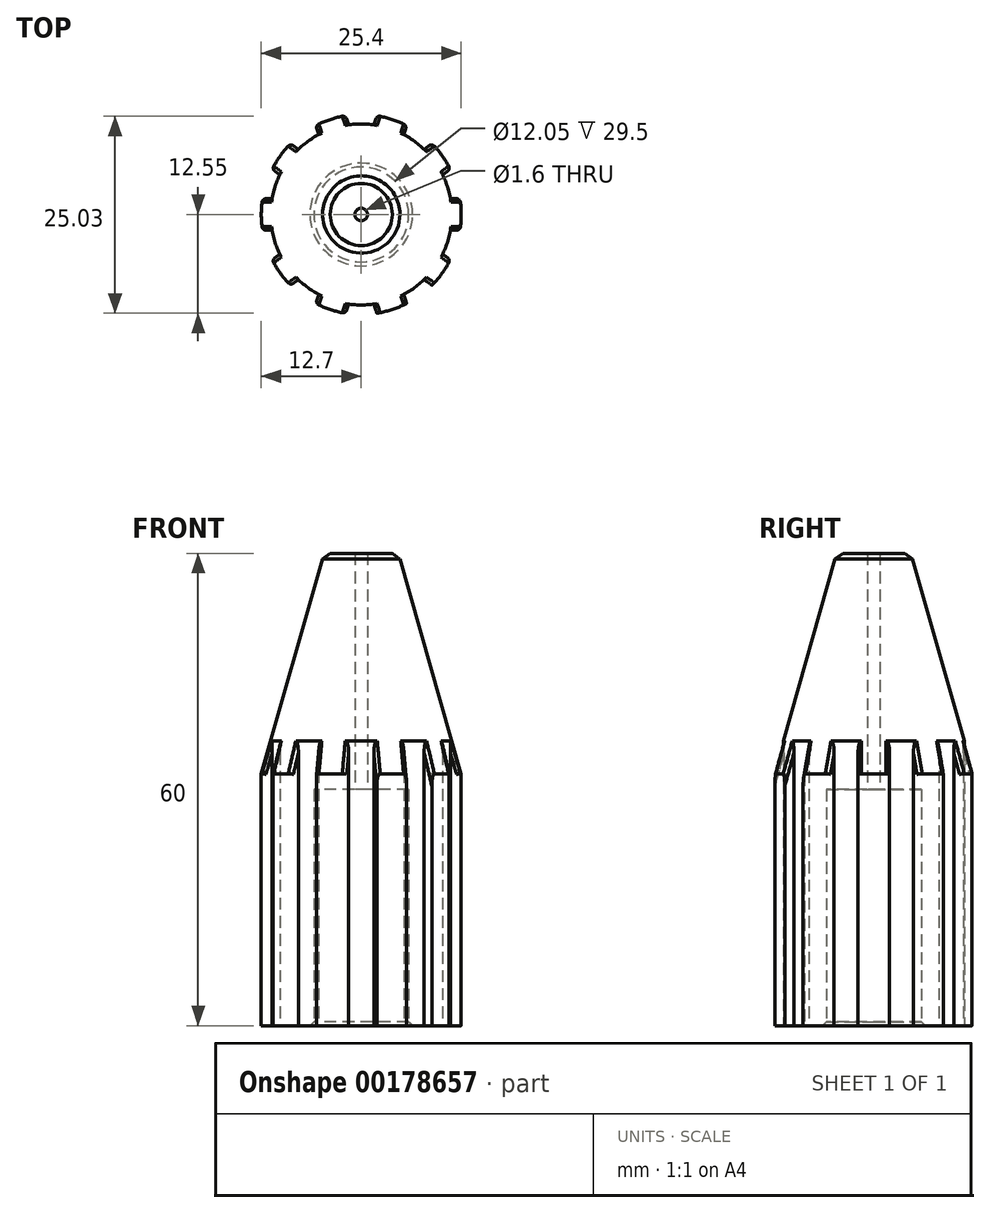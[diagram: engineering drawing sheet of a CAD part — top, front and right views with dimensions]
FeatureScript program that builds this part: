
annotation { "Feature Type Name" : "Feature", "Feature Type Description" : "" }
export const myFeature = defineFeature(function(context is Context, id is Id, definition is map)
    precondition{}
    {
        {
            var Q0;
            Q0=qCreatedBy(makeId("Top.planeOp"),FACE);
            var sketch = newSketch(context, id + "F0", { "sketchPlane" : qUnion([Q0])});
            skCircle(sketch, "E0", {"center": v(0, 0) * mm, "radius": 6.03 * mm});
            skArc(sketch, "E1", {"start": v(12.54, -2) * mm, "mid": v(12.7, 0) * mm, "end": v(12.54, 2) * mm});
            skArc(sketch, "E2", {"start": v(11.32, 2) * mm, "mid": v(10.94, 3.55) * mm, "end": v(10.34, 5.04) * mm});
            skLineSegment(sketch, "E3", {"start": v(11.32, -2) * mm, "end": v(12.54, -2) * mm});
            skLineSegment(sketch, "E4", {"start": v(11.32, 2) * mm, "end": v(12.54, 2) * mm});
            skLineSegment(sketch, "E5.1.0", {"start": v(10.34, -5.04) * mm, "end": v(11.32, -5.75) * mm});
            skArc(sketch, "E5.1.1", {"start": v(8.97, -8.99) * mm, "mid": v(10.27, -7.46) * mm, "end": v(11.32, -5.75) * mm});
            skLineSegment(sketch, "E5.1.2", {"start": v(7.99, -8.27) * mm, "end": v(8.97, -8.99) * mm});
            skLineSegment(sketch, "E5.2.0", {"start": v(5.4, -10.15) * mm, "end": v(5.78, -11.3) * mm});
            skArc(sketch, "E5.2.1", {"start": v(1.97, -12.55) * mm, "mid": v(3.92, -12.08) * mm, "end": v(5.78, -11.3) * mm});
            skLineSegment(sketch, "E5.2.2", {"start": v(1.6, -11.39) * mm, "end": v(1.97, -12.55) * mm});
            skLineSegment(sketch, "E5.3.0", {"start": v(-1.6, -11.39) * mm, "end": v(-1.97, -12.55) * mm});
            skArc(sketch, "E5.3.1", {"start": v(-5.78, -11.3) * mm, "mid": v(-3.92, -12.08) * mm, "end": v(-1.97, -12.55) * mm});
            skLineSegment(sketch, "E5.3.2", {"start": v(-5.4, -10.15) * mm, "end": v(-5.78, -11.3) * mm});
            skLineSegment(sketch, "E5.4.0", {"start": v(-7.99, -8.27) * mm, "end": v(-8.97, -8.99) * mm});
            skArc(sketch, "E5.4.1", {"start": v(-11.32, -5.75) * mm, "mid": v(-10.27, -7.46) * mm, "end": v(-8.97, -8.99) * mm});
            skLineSegment(sketch, "E5.4.2", {"start": v(-10.34, -5.04) * mm, "end": v(-11.32, -5.75) * mm});
            skLineSegment(sketch, "E5.5.0", {"start": v(-11.32, -2) * mm, "end": v(-12.54, -2) * mm});
            skArc(sketch, "E5.5.1", {"start": v(-12.54, 2) * mm, "mid": v(-12.7, 0) * mm, "end": v(-12.54, -2) * mm});
            skLineSegment(sketch, "E5.5.2", {"start": v(-11.32, 2) * mm, "end": v(-12.54, 2) * mm});
            skLineSegment(sketch, "E5.anchor1", {"start": v(0, 0) * mm, "end": v(11.32, 2) * mm, "construction": true});
            skLineSegment(sketch, "E5.anchor2", {"start": v(0, 0) * mm, "end": v(-11.32, -2) * mm, "construction": true});
            skLineSegment(sketch, "E6.MirrorCS", {"start": v(-10.34, 5.04) * mm, "end": v(-11.32, 5.75) * mm});
            skArc(sketch, "E7.MirrorCS", {"start": v(-11.32, 5.75) * mm, "mid": v(-10.27, 7.46) * mm, "end": v(-8.97, 8.99) * mm});
            skLineSegment(sketch, "E8.MirrorCS", {"start": v(-7.99, 8.27) * mm, "end": v(-8.97, 8.99) * mm});
            skLineSegment(sketch, "E9.MirrorCS", {"start": v(-5.4, 10.15) * mm, "end": v(-5.78, 11.3) * mm});
            skArc(sketch, "E10.MirrorCS", {"start": v(-5.78, 11.3) * mm, "mid": v(-3.92, 12.08) * mm, "end": v(-1.97, 12.55) * mm});
            skLineSegment(sketch, "E11.MirrorCS", {"start": v(-1.6, 11.39) * mm, "end": v(-1.97, 12.55) * mm});
            skLineSegment(sketch, "E12.MirrorCS", {"start": v(1.6, 11.39) * mm, "end": v(1.97, 12.55) * mm});
            skArc(sketch, "E13.MirrorCS", {"start": v(1.97, 12.55) * mm, "mid": v(3.92, 12.08) * mm, "end": v(5.78, 11.3) * mm});
            skLineSegment(sketch, "E14.MirrorCS", {"start": v(5.4, 10.15) * mm, "end": v(5.78, 11.3) * mm});
            skLineSegment(sketch, "E15.MirrorCS", {"start": v(10.34, 5.04) * mm, "end": v(11.32, 5.75) * mm});
            skLineSegment(sketch, "E16.MirrorCS", {"start": v(7.99, 8.27) * mm, "end": v(8.97, 8.99) * mm});
            skArc(sketch, "E17.MirrorCS", {"start": v(8.97, 8.99) * mm, "mid": v(10.27, 7.46) * mm, "end": v(11.32, 5.75) * mm});
            skArc(sketch, "E18.trimOffspring", {"start": v(10.34, -5.04) * mm, "mid": v(10.94, -3.55) * mm, "end": v(11.32, -2) * mm});
            skArc(sketch, "E19.trimOffspring", {"start": v(5.4, -10.15) * mm, "mid": v(6.76, -9.3) * mm, "end": v(7.99, -8.27) * mm});
            skArc(sketch, "E20.trimOffspring", {"start": v(-1.6, -11.39) * mm, "mid": v(0, -11.5) * mm, "end": v(1.6, -11.39) * mm});
            skArc(sketch, "E21.trimOffspring", {"start": v(-7.99, -8.27) * mm, "mid": v(-6.76, -9.3) * mm, "end": v(-5.4, -10.15) * mm});
            skArc(sketch, "E22.trimOffspring", {"start": v(-11.32, -2) * mm, "mid": v(-10.94, -3.55) * mm, "end": v(-10.34, -5.04) * mm});
            skArc(sketch, "E23.trimOffspring", {"start": v(-10.34, 5.04) * mm, "mid": v(-10.94, 3.55) * mm, "end": v(-11.32, 2) * mm});
            skArc(sketch, "E24.trimOffspring", {"start": v(-5.4, 10.15) * mm, "mid": v(-6.76, 9.3) * mm, "end": v(-7.99, 8.27) * mm});
            skArc(sketch, "E25.trimOffspring", {"start": v(1.6, 11.39) * mm, "mid": v(0, 11.5) * mm, "end": v(-1.6, 11.39) * mm});
            skArc(sketch, "E26.trimOffspring", {"start": v(7.99, 8.27) * mm, "mid": v(6.76, 9.3) * mm, "end": v(5.4, 10.15) * mm});
            skSolve(sketch);
        }
        {
            var Q0;
            Q0=makeQuery(id+"F0.imprint","IMPRINT",FACE,{"disambiguationData":[TD([[makeQuery(id+"F0.imprint","IMPRINT",EDGE,{"derivedFrom":sQuery(id+"F0.wireOp",EDGE,"E0")}),-1.0]])]});
            extrude(context, id + "F1", {"entities" : qUnion([Q0]), "depth" : 30 * mm});
        }
        {
            var Q0;
            Q0=makeQuery(id+"F1.opExtrude","CAP_FACE",FACE,{"disambiguationData":[OSD([sQuery(id+"F0.wireOp",EDGE,"E0"),sQuery(id+"F0.wireOp",EDGE,"E1")])],"isStart":false});
            var sketch = newSketch(context, id + "F2", { "sketchPlane" : qUnion([Q0])});
            skCircle(sketch, "E27.0", {"center": v(0, 0) * mm, "radius": 12.7 * mm});
            skCircle(sketch, "E28", {"center": v(0, 0) * mm, "radius": 0.8 * mm});
            skSolve(sketch);
        }
        {
            var Q0;
            Q0 = qSketchRegion(id + "F2", true);
            extrude(context, id + "F3", {"entities" : qUnion([Q0]), "operationType" : NewBodyOperationType.ADD, "depth" : 30 * mm});
        }
        {
            var Q0;
            Q0=makeQuery(id+"F3.opExtrude","CAP_EDGE",EDGE,{"disambiguationData":[OSD([sQuery(id+"F2.wireOp",EDGE,"E27.0")])],"isStart":false});
            chamfer(context, id + "F4", {"entities" : qUnion([Q0]), "chamferType" : ChamferType.TWO_OFFSETS, "width1" : 8 * mm, "oppositeDirection" : false, "width2" : 28 * mm, "tangentPropagation" : true});
        }
        {
            var Q0;
            Q0=makeQuery(id+"F1.opExtrude","CAP_EDGE",EDGE,{"disambiguationData":[OSD([sQuery(id+"F0.wireOp",EDGE,"E0")])],"isStart":true});
            chamfer(context, id + "F5", {"entities" : qUnion([Q0]), "width" : .5 * mm, "tangentPropagation" : true});
        }
        {
            var Q0;
            {var subQ0=sQuery(id+"F2.wireOp",EDGE,"E27.0");Q0=makeQuery(id+"F4.opChamfer","BLEND_EDGE",EDGE,{"blendedFrom":[makeQuery(id+"F3.opExtrude","CAP_EDGE",EDGE,{"disambiguationData":[OSD([subQ0])],"isStart":false}),makeQuery(id+"F3.opExtrude","CAP_FACE",FACE,{"disambiguationData":[OSD([subQ0,sQuery(id+"F2.wireOp",EDGE,"E28")])],"isStart":false})],"blendedInto":[makeQuery(id+"F3.opExtrude","CAP_FACE",FACE,{"disambiguationData":[OSD([subQ0,sQuery(id+"F2.wireOp",EDGE,"E28")])],"isStart":false})]});}
            chamfer(context, id + "F6", {"entities" : qUnion([Q0]), "width" : 1 * mm, "tangentPropagation" : true});
        }
        {
            var Q0;
            {var subQ1=makeQuery(id+"F1.opExtrude","CAP_EDGE",EDGE,{"disambiguationData":[OSD([sQuery(id+"F0.wireOp",EDGE,"E5.1.2")])],"isStart":false});Q0=makeQuery(id+"F2.imprint","IMPRINT",FACE,{"disambiguationData":[TD([[makeQuery(id+"F2.imprint","IMPRINT",EDGE,{"derivedFrom":subQ1}),-1.0]])]});}
            extrude(context, id + "F7", {"entities" : qUnion([Q0]), "operationType" : NewBodyOperationType.REMOVE, "depth" : 25 * mm});
        }
        {
            var Q0;
            {var subQ1=makeQuery(id+"F1.opExtrude","CAP_EDGE",EDGE,{"disambiguationData":[OSD([sQuery(id+"F0.wireOp",EDGE,"E5.2.2")])],"isStart":false});Q0=makeQuery(id+"F2.imprint","IMPRINT",FACE,{"disambiguationData":[TD([[makeQuery(id+"F2.imprint","IMPRINT",EDGE,{"derivedFrom":subQ1}),-1.0]])]});}
            var Q1;
            {var subQ1=makeQuery(id+"F1.opExtrude","CAP_EDGE",EDGE,{"disambiguationData":[OSD([sQuery(id+"F0.wireOp",EDGE,"E3")])],"isStart":false});Q1=makeQuery(id+"F2.imprint","IMPRINT",FACE,{"disambiguationData":[TD([[makeQuery(id+"F2.imprint","IMPRINT",EDGE,{"derivedFrom":subQ1}),-1.0]])]});}
            var Q2;
            {var subQ1=makeQuery(id+"F1.opExtrude","CAP_EDGE",EDGE,{"disambiguationData":[OSD([sQuery(id+"F0.wireOp",EDGE,"E5.3.2")])],"isStart":false});Q2=makeQuery(id+"F2.imprint","IMPRINT",FACE,{"disambiguationData":[TD([[makeQuery(id+"F2.imprint","IMPRINT",EDGE,{"derivedFrom":subQ1}),-1.0]])]});}
            var Q3;
            {var subQ1=makeQuery(id+"F1.opExtrude","CAP_EDGE",EDGE,{"disambiguationData":[OSD([sQuery(id+"F0.wireOp",EDGE,"E5.4.2")])],"isStart":false});Q3=makeQuery(id+"F2.imprint","IMPRINT",FACE,{"disambiguationData":[TD([[makeQuery(id+"F2.imprint","IMPRINT",EDGE,{"derivedFrom":subQ1}),-1.0]])]});}
            var Q4;
            {var subQ1=makeQuery(id+"F1.opExtrude","CAP_EDGE",EDGE,{"disambiguationData":[OSD([sQuery(id+"F0.wireOp",EDGE,"E5.5.2")])],"isStart":false});Q4=makeQuery(id+"F2.imprint","IMPRINT",FACE,{"disambiguationData":[TD([[makeQuery(id+"F2.imprint","IMPRINT",EDGE,{"derivedFrom":subQ1}),-1.0]])]});}
            var Q5;
            {var subQ1=makeQuery(id+"F1.opExtrude","CAP_EDGE",EDGE,{"disambiguationData":[OSD([sQuery(id+"F0.wireOp",EDGE,"E8.MirrorCS")])],"isStart":false});Q5=makeQuery(id+"F2.imprint","IMPRINT",FACE,{"disambiguationData":[TD([[makeQuery(id+"F2.imprint","IMPRINT",EDGE,{"derivedFrom":subQ1}),-1.0]])]});}
            var Q6;
            {var subQ1=makeQuery(id+"F1.opExtrude","CAP_EDGE",EDGE,{"disambiguationData":[OSD([sQuery(id+"F0.wireOp",EDGE,"E11.MirrorCS")])],"isStart":false});Q6=makeQuery(id+"F2.imprint","IMPRINT",FACE,{"disambiguationData":[TD([[makeQuery(id+"F2.imprint","IMPRINT",EDGE,{"derivedFrom":subQ1}),-1.0]])]});}
            var Q7;
            {var subQ1=makeQuery(id+"F1.opExtrude","CAP_EDGE",EDGE,{"disambiguationData":[OSD([sQuery(id+"F0.wireOp",EDGE,"E14.MirrorCS")])],"isStart":false});Q7=makeQuery(id+"F2.imprint","IMPRINT",FACE,{"disambiguationData":[TD([[makeQuery(id+"F2.imprint","IMPRINT",EDGE,{"derivedFrom":subQ1}),-1.0]])]});}
            var Q8;
            Q8=makeQuery(id+"F2.imprint","IMPRINT",FACE,{"disambiguationData":[TD([[makeQuery(id+"F2.imprint","IMPRINT",EDGE,{"derivedFrom":makeQuery(id+"F1.opExtrude","CAP_EDGE",EDGE,{"disambiguationData":[OSD([sQuery(id+"F0.wireOp",EDGE,"E2")])],"isStart":false})}),-1.0]])]});
            extrude(context, id + "F8", {"entities" : qUnion([Q0, Q1, Q2, Q3, Q4, Q5, Q6, Q7, Q8]), "operationType" : NewBodyOperationType.REMOVE, "depth" : 25 * mm});
        }
        {
            var Q0;
            {var subQ0=sQuery(id+"F0.wireOp",EDGE,"E5.2.0");Q0=makeQuery(id+"F7.boolean.opBoolean","MERGE",EDGE,{"derivedFrom":[makeQuery(id+"F1.opExtrude","SWEPT_EDGE",EDGE,{"disambiguationData":[OSD([subQ0,sQuery(id+"F0.wireOp",EDGE,"E5.2.1")])]}),makeQuery(id+"F7.opExtrude","SWEPT_EDGE",EDGE,{"disambiguationData":[OSD([subQ0,sQuery(id+"F2.wireOp",EDGE,"E27.0")])]})]});}
            var Q1;
            Q1=makeQuery(id+"F7.boolean.opBoolean","INTERSECT",EDGE,{"derivedFrom":[makeQuery(id+"F4.opChamfer","BLEND_FACE",FACE,{"disambiguationData":[OSD([sQuery(id+"F2.wireOp",EDGE,"E27.0")])]}),makeQuery(id+"F7.opExtrude","SWEPT_FACE",FACE,{"disambiguationData":[OSD([sQuery(id+"F0.wireOp",EDGE,"E5.2.0")])]})]});
            var Q2;
            {var subQ0=sQuery(id+"F0.wireOp",EDGE,"E5.1.2");Q2=makeQuery(id+"F7.boolean.opBoolean","MERGE",EDGE,{"derivedFrom":[makeQuery(id+"F1.opExtrude","SWEPT_EDGE",EDGE,{"disambiguationData":[OSD([sQuery(id+"F0.wireOp",EDGE,"E5.1.1"),subQ0])]}),makeQuery(id+"F7.opExtrude","SWEPT_EDGE",EDGE,{"disambiguationData":[OSD([subQ0,sQuery(id+"F2.wireOp",EDGE,"E27.0")])]})]});}
            var Q3;
            Q3=makeQuery(id+"F7.boolean.opBoolean","INTERSECT",EDGE,{"derivedFrom":[makeQuery(id+"F4.opChamfer","BLEND_FACE",FACE,{"disambiguationData":[OSD([sQuery(id+"F2.wireOp",EDGE,"E27.0")])]}),makeQuery(id+"F7.opExtrude","SWEPT_FACE",FACE,{"disambiguationData":[OSD([sQuery(id+"F0.wireOp",EDGE,"E5.1.2")])]})]});
            var Q4;
            {var subQ0=sQuery(id+"F0.wireOp",EDGE,"E5.2.2");Q4=makeQuery(id+"F8.boolean.opBoolean","MERGE",EDGE,{"derivedFrom":[makeQuery(id+"F1.opExtrude","SWEPT_EDGE",EDGE,{"disambiguationData":[OSD([sQuery(id+"F0.wireOp",EDGE,"E5.2.1"),subQ0])]}),makeQuery(id+"F8.opExtrude","SWEPT_EDGE",EDGE,{"disambiguationData":[OSD([subQ0,sQuery(id+"F2.wireOp",EDGE,"E27.0")])]})]});}
            var Q5;
            Q5=makeQuery(id+"F8.boolean.opBoolean","INTERSECT",EDGE,{"derivedFrom":[makeQuery(id+"F4.opChamfer","BLEND_FACE",FACE,{"disambiguationData":[OSD([sQuery(id+"F2.wireOp",EDGE,"E27.0")])]}),makeQuery(id+"F8.opExtrude","SWEPT_FACE",FACE,{"disambiguationData":[OSD([sQuery(id+"F0.wireOp",EDGE,"E5.2.2")])]})]});
            var Q6;
            Q6=makeQuery(id+"F8.boolean.opBoolean","INTERSECT",EDGE,{"derivedFrom":[makeQuery(id+"F4.opChamfer","BLEND_FACE",FACE,{"disambiguationData":[OSD([sQuery(id+"F2.wireOp",EDGE,"E27.0")])]}),makeQuery(id+"F8.opExtrude","SWEPT_FACE",FACE,{"disambiguationData":[OSD([sQuery(id+"F0.wireOp",EDGE,"E5.3.0")])]})]});
            var Q7;
            {var subQ0=sQuery(id+"F0.wireOp",EDGE,"E5.3.0");Q7=makeQuery(id+"F8.boolean.opBoolean","MERGE",EDGE,{"derivedFrom":[makeQuery(id+"F1.opExtrude","SWEPT_EDGE",EDGE,{"disambiguationData":[OSD([subQ0,sQuery(id+"F0.wireOp",EDGE,"E5.3.1")])]}),makeQuery(id+"F8.opExtrude","SWEPT_EDGE",EDGE,{"disambiguationData":[OSD([subQ0,sQuery(id+"F2.wireOp",EDGE,"E27.0")])]})]});}
            var Q8;
            Q8=makeQuery(id+"F8.boolean.opBoolean","INTERSECT",EDGE,{"derivedFrom":[makeQuery(id+"F4.opChamfer","BLEND_FACE",FACE,{"disambiguationData":[OSD([sQuery(id+"F2.wireOp",EDGE,"E27.0")])]}),makeQuery(id+"F8.opExtrude","SWEPT_FACE",FACE,{"disambiguationData":[OSD([sQuery(id+"F0.wireOp",EDGE,"E5.3.2")])]})]});
            var Q9;
            {var subQ0=sQuery(id+"F0.wireOp",EDGE,"E5.3.2");Q9=makeQuery(id+"F8.boolean.opBoolean","MERGE",EDGE,{"derivedFrom":[makeQuery(id+"F1.opExtrude","SWEPT_EDGE",EDGE,{"disambiguationData":[OSD([sQuery(id+"F0.wireOp",EDGE,"E5.3.1"),subQ0])]}),makeQuery(id+"F8.opExtrude","SWEPT_EDGE",EDGE,{"disambiguationData":[OSD([subQ0,sQuery(id+"F2.wireOp",EDGE,"E27.0")])]})]});}
            var Q10;
            Q10=makeQuery(id+"F8.boolean.opBoolean","INTERSECT",EDGE,{"derivedFrom":[makeQuery(id+"F4.opChamfer","BLEND_FACE",FACE,{"disambiguationData":[OSD([sQuery(id+"F2.wireOp",EDGE,"E27.0")])]}),makeQuery(id+"F8.opExtrude","SWEPT_FACE",FACE,{"disambiguationData":[OSD([sQuery(id+"F0.wireOp",EDGE,"E5.4.0")])]})]});
            var Q11;
            {var subQ0=sQuery(id+"F0.wireOp",EDGE,"E5.4.0");Q11=makeQuery(id+"F8.boolean.opBoolean","MERGE",EDGE,{"derivedFrom":[makeQuery(id+"F1.opExtrude","SWEPT_EDGE",EDGE,{"disambiguationData":[OSD([subQ0,sQuery(id+"F0.wireOp",EDGE,"E5.4.1")])]}),makeQuery(id+"F8.opExtrude","SWEPT_EDGE",EDGE,{"disambiguationData":[OSD([subQ0,sQuery(id+"F2.wireOp",EDGE,"E27.0")])]})]});}
            var Q12;
            Q12=makeQuery(id+"F8.boolean.opBoolean","INTERSECT",EDGE,{"derivedFrom":[makeQuery(id+"F4.opChamfer","BLEND_FACE",FACE,{"disambiguationData":[OSD([sQuery(id+"F2.wireOp",EDGE,"E27.0")])]}),makeQuery(id+"F8.opExtrude","SWEPT_FACE",FACE,{"disambiguationData":[OSD([sQuery(id+"F0.wireOp",EDGE,"E5.5.0")])]})]});
            var Q13;
            {var subQ0=sQuery(id+"F0.wireOp",EDGE,"E5.5.0");Q13=makeQuery(id+"F8.boolean.opBoolean","MERGE",EDGE,{"derivedFrom":[makeQuery(id+"F1.opExtrude","SWEPT_EDGE",EDGE,{"disambiguationData":[OSD([subQ0,sQuery(id+"F0.wireOp",EDGE,"E5.5.1")])]}),makeQuery(id+"F8.opExtrude","SWEPT_EDGE",EDGE,{"disambiguationData":[OSD([subQ0,sQuery(id+"F2.wireOp",EDGE,"E27.0")])]})]});}
            var Q14;
            Q14=makeQuery(id+"F8.boolean.opBoolean","INTERSECT",EDGE,{"derivedFrom":[makeQuery(id+"F4.opChamfer","BLEND_FACE",FACE,{"disambiguationData":[OSD([sQuery(id+"F2.wireOp",EDGE,"E27.0")])]}),makeQuery(id+"F8.opExtrude","SWEPT_FACE",FACE,{"disambiguationData":[OSD([sQuery(id+"F0.wireOp",EDGE,"E5.4.2")])]})]});
            var Q15;
            {var subQ0=sQuery(id+"F0.wireOp",EDGE,"E5.4.2");Q15=makeQuery(id+"F8.boolean.opBoolean","MERGE",EDGE,{"derivedFrom":[makeQuery(id+"F1.opExtrude","SWEPT_EDGE",EDGE,{"disambiguationData":[OSD([sQuery(id+"F0.wireOp",EDGE,"E5.4.1"),subQ0])]}),makeQuery(id+"F8.opExtrude","SWEPT_EDGE",EDGE,{"disambiguationData":[OSD([subQ0,sQuery(id+"F2.wireOp",EDGE,"E27.0")])]})]});}
            var Q16;
            Q16=makeQuery(id+"F8.boolean.opBoolean","INTERSECT",EDGE,{"derivedFrom":[makeQuery(id+"F4.opChamfer","BLEND_FACE",FACE,{"disambiguationData":[OSD([sQuery(id+"F2.wireOp",EDGE,"E27.0")])]}),makeQuery(id+"F8.opExtrude","SWEPT_FACE",FACE,{"disambiguationData":[OSD([sQuery(id+"F0.wireOp",EDGE,"E6.MirrorCS")])]})]});
            var Q17;
            {var subQ0=sQuery(id+"F0.wireOp",EDGE,"E6.MirrorCS");Q17=makeQuery(id+"F8.boolean.opBoolean","MERGE",EDGE,{"derivedFrom":[makeQuery(id+"F1.opExtrude","SWEPT_EDGE",EDGE,{"disambiguationData":[OSD([subQ0,sQuery(id+"F0.wireOp",EDGE,"E7.MirrorCS")])]}),makeQuery(id+"F8.opExtrude","SWEPT_EDGE",EDGE,{"disambiguationData":[OSD([subQ0,sQuery(id+"F2.wireOp",EDGE,"E27.0")])]})]});}
            var Q18;
            {var subQ0=sQuery(id+"F0.wireOp",EDGE,"E5.5.2");Q18=makeQuery(id+"F8.boolean.opBoolean","MERGE",EDGE,{"derivedFrom":[makeQuery(id+"F1.opExtrude","SWEPT_EDGE",EDGE,{"disambiguationData":[OSD([sQuery(id+"F0.wireOp",EDGE,"E5.5.1"),subQ0])]}),makeQuery(id+"F8.opExtrude","SWEPT_EDGE",EDGE,{"disambiguationData":[OSD([subQ0,sQuery(id+"F2.wireOp",EDGE,"E27.0")])]})]});}
            var Q19;
            Q19=makeQuery(id+"F8.boolean.opBoolean","INTERSECT",EDGE,{"derivedFrom":[makeQuery(id+"F4.opChamfer","BLEND_FACE",FACE,{"disambiguationData":[OSD([sQuery(id+"F2.wireOp",EDGE,"E27.0")])]}),makeQuery(id+"F8.opExtrude","SWEPT_FACE",FACE,{"disambiguationData":[OSD([sQuery(id+"F0.wireOp",EDGE,"E5.5.2")])]})]});
            var Q20;
            Q20=makeQuery(id+"F8.boolean.opBoolean","INTERSECT",EDGE,{"derivedFrom":[makeQuery(id+"F4.opChamfer","BLEND_FACE",FACE,{"disambiguationData":[OSD([sQuery(id+"F2.wireOp",EDGE,"E27.0")])]}),makeQuery(id+"F8.opExtrude","SWEPT_FACE",FACE,{"disambiguationData":[OSD([sQuery(id+"F0.wireOp",EDGE,"E8.MirrorCS")])]})]});
            var Q21;
            {var subQ0=sQuery(id+"F0.wireOp",EDGE,"E8.MirrorCS");Q21=makeQuery(id+"F8.boolean.opBoolean","MERGE",EDGE,{"derivedFrom":[makeQuery(id+"F1.opExtrude","SWEPT_EDGE",EDGE,{"disambiguationData":[OSD([sQuery(id+"F0.wireOp",EDGE,"E7.MirrorCS"),subQ0])]}),makeQuery(id+"F8.opExtrude","SWEPT_EDGE",EDGE,{"disambiguationData":[OSD([subQ0,sQuery(id+"F2.wireOp",EDGE,"E27.0")])]})]});}
            var Q22;
            Q22=makeQuery(id+"F8.boolean.opBoolean","INTERSECT",EDGE,{"derivedFrom":[makeQuery(id+"F4.opChamfer","BLEND_FACE",FACE,{"disambiguationData":[OSD([sQuery(id+"F2.wireOp",EDGE,"E27.0")])]}),makeQuery(id+"F8.opExtrude","SWEPT_FACE",FACE,{"disambiguationData":[OSD([sQuery(id+"F0.wireOp",EDGE,"E9.MirrorCS")])]})]});
            var Q23;
            {var subQ0=sQuery(id+"F0.wireOp",EDGE,"E9.MirrorCS");Q23=makeQuery(id+"F8.boolean.opBoolean","MERGE",EDGE,{"derivedFrom":[makeQuery(id+"F1.opExtrude","SWEPT_EDGE",EDGE,{"disambiguationData":[OSD([subQ0,sQuery(id+"F0.wireOp",EDGE,"E10.MirrorCS")])]}),makeQuery(id+"F8.opExtrude","SWEPT_EDGE",EDGE,{"disambiguationData":[OSD([subQ0,sQuery(id+"F2.wireOp",EDGE,"E27.0")])]})]});}
            var Q24;
            Q24=makeQuery(id+"F8.boolean.opBoolean","INTERSECT",EDGE,{"derivedFrom":[makeQuery(id+"F4.opChamfer","BLEND_FACE",FACE,{"disambiguationData":[OSD([sQuery(id+"F2.wireOp",EDGE,"E27.0")])]}),makeQuery(id+"F8.opExtrude","SWEPT_FACE",FACE,{"disambiguationData":[OSD([sQuery(id+"F0.wireOp",EDGE,"E11.MirrorCS")])]})]});
            var Q25;
            {var subQ0=sQuery(id+"F0.wireOp",EDGE,"E11.MirrorCS");Q25=makeQuery(id+"F8.boolean.opBoolean","MERGE",EDGE,{"derivedFrom":[makeQuery(id+"F1.opExtrude","SWEPT_EDGE",EDGE,{"disambiguationData":[OSD([sQuery(id+"F0.wireOp",EDGE,"E10.MirrorCS"),subQ0])]}),makeQuery(id+"F8.opExtrude","SWEPT_EDGE",EDGE,{"disambiguationData":[OSD([subQ0,sQuery(id+"F2.wireOp",EDGE,"E27.0")])]})]});}
            var Q26;
            Q26=makeQuery(id+"F8.boolean.opBoolean","INTERSECT",EDGE,{"derivedFrom":[makeQuery(id+"F4.opChamfer","BLEND_FACE",FACE,{"disambiguationData":[OSD([sQuery(id+"F2.wireOp",EDGE,"E27.0")])]}),makeQuery(id+"F8.opExtrude","SWEPT_FACE",FACE,{"disambiguationData":[OSD([sQuery(id+"F0.wireOp",EDGE,"E12.MirrorCS")])]})]});
            var Q27;
            {var subQ0=sQuery(id+"F0.wireOp",EDGE,"E12.MirrorCS");Q27=makeQuery(id+"F8.boolean.opBoolean","MERGE",EDGE,{"derivedFrom":[makeQuery(id+"F1.opExtrude","SWEPT_EDGE",EDGE,{"disambiguationData":[OSD([subQ0,sQuery(id+"F0.wireOp",EDGE,"E13.MirrorCS")])]}),makeQuery(id+"F8.opExtrude","SWEPT_EDGE",EDGE,{"disambiguationData":[OSD([subQ0,sQuery(id+"F2.wireOp",EDGE,"E27.0")])]})]});}
            var Q28;
            Q28=makeQuery(id+"F8.boolean.opBoolean","INTERSECT",EDGE,{"derivedFrom":[makeQuery(id+"F4.opChamfer","BLEND_FACE",FACE,{"disambiguationData":[OSD([sQuery(id+"F2.wireOp",EDGE,"E27.0")])]}),makeQuery(id+"F8.opExtrude","SWEPT_FACE",FACE,{"disambiguationData":[OSD([sQuery(id+"F0.wireOp",EDGE,"E14.MirrorCS")])]})]});
            var Q29;
            {var subQ0=sQuery(id+"F0.wireOp",EDGE,"E14.MirrorCS");Q29=makeQuery(id+"F8.boolean.opBoolean","MERGE",EDGE,{"derivedFrom":[makeQuery(id+"F1.opExtrude","SWEPT_EDGE",EDGE,{"disambiguationData":[OSD([sQuery(id+"F0.wireOp",EDGE,"E13.MirrorCS"),subQ0])]}),makeQuery(id+"F8.opExtrude","SWEPT_EDGE",EDGE,{"disambiguationData":[OSD([subQ0,sQuery(id+"F2.wireOp",EDGE,"E27.0")])]})]});}
            var Q30;
            Q30=makeQuery(id+"F8.boolean.opBoolean","INTERSECT",EDGE,{"derivedFrom":[makeQuery(id+"F4.opChamfer","BLEND_FACE",FACE,{"disambiguationData":[OSD([sQuery(id+"F2.wireOp",EDGE,"E27.0")])]}),makeQuery(id+"F8.opExtrude","SWEPT_FACE",FACE,{"disambiguationData":[OSD([sQuery(id+"F0.wireOp",EDGE,"E16.MirrorCS")])]})]});
            var Q31;
            {var subQ0=sQuery(id+"F0.wireOp",EDGE,"E16.MirrorCS");Q31=makeQuery(id+"F8.boolean.opBoolean","MERGE",EDGE,{"derivedFrom":[makeQuery(id+"F1.opExtrude","SWEPT_EDGE",EDGE,{"disambiguationData":[OSD([subQ0,sQuery(id+"F0.wireOp",EDGE,"E17.MirrorCS")])]}),makeQuery(id+"F8.opExtrude","SWEPT_EDGE",EDGE,{"disambiguationData":[OSD([subQ0,sQuery(id+"F2.wireOp",EDGE,"E27.0")])]})]});}
            var Q32;
            Q32=makeQuery(id+"F8.boolean.opBoolean","INTERSECT",EDGE,{"derivedFrom":[makeQuery(id+"F4.opChamfer","BLEND_FACE",FACE,{"disambiguationData":[OSD([sQuery(id+"F2.wireOp",EDGE,"E27.0")])]}),makeQuery(id+"F8.opExtrude","SWEPT_FACE",FACE,{"disambiguationData":[OSD([sQuery(id+"F0.wireOp",EDGE,"E4")])]})]});
            var Q33;
            {var subQ0=sQuery(id+"F0.wireOp",EDGE,"E4");Q33=makeQuery(id+"F8.boolean.opBoolean","MERGE",EDGE,{"derivedFrom":[makeQuery(id+"F1.opExtrude","SWEPT_EDGE",EDGE,{"disambiguationData":[OSD([sQuery(id+"F0.wireOp",EDGE,"E1"),subQ0])]}),makeQuery(id+"F8.opExtrude","SWEPT_EDGE",EDGE,{"disambiguationData":[OSD([subQ0,sQuery(id+"F2.wireOp",EDGE,"E27.0")])]})]});}
            var Q34;
            Q34=makeQuery(id+"F8.boolean.opBoolean","INTERSECT",EDGE,{"derivedFrom":[makeQuery(id+"F4.opChamfer","BLEND_FACE",FACE,{"disambiguationData":[OSD([sQuery(id+"F2.wireOp",EDGE,"E27.0")])]}),makeQuery(id+"F8.opExtrude","SWEPT_FACE",FACE,{"disambiguationData":[OSD([sQuery(id+"F0.wireOp",EDGE,"E15.MirrorCS")])]})]});
            var Q35;
            {var subQ0=sQuery(id+"F0.wireOp",EDGE,"E15.MirrorCS");Q35=makeQuery(id+"F8.boolean.opBoolean","MERGE",EDGE,{"derivedFrom":[makeQuery(id+"F1.opExtrude","SWEPT_EDGE",EDGE,{"disambiguationData":[OSD([subQ0,sQuery(id+"F0.wireOp",EDGE,"E17.MirrorCS")])]}),makeQuery(id+"F8.opExtrude","SWEPT_EDGE",EDGE,{"disambiguationData":[OSD([subQ0,sQuery(id+"F2.wireOp",EDGE,"E27.0")])]})]});}
            var Q36;
            Q36=makeQuery(id+"F8.boolean.opBoolean","INTERSECT",EDGE,{"derivedFrom":[makeQuery(id+"F4.opChamfer","BLEND_FACE",FACE,{"disambiguationData":[OSD([sQuery(id+"F2.wireOp",EDGE,"E27.0")])]}),makeQuery(id+"F8.opExtrude","SWEPT_FACE",FACE,{"disambiguationData":[OSD([sQuery(id+"F0.wireOp",EDGE,"E3")])]})]});
            var Q37;
            {var subQ0=sQuery(id+"F0.wireOp",EDGE,"E3");Q37=makeQuery(id+"F8.boolean.opBoolean","MERGE",EDGE,{"derivedFrom":[makeQuery(id+"F1.opExtrude","SWEPT_EDGE",EDGE,{"disambiguationData":[OSD([sQuery(id+"F0.wireOp",EDGE,"E1"),subQ0])]}),makeQuery(id+"F8.opExtrude","SWEPT_EDGE",EDGE,{"disambiguationData":[OSD([subQ0,sQuery(id+"F2.wireOp",EDGE,"E27.0")])]})]});}
            var Q38;
            Q38=makeQuery(id+"F8.boolean.opBoolean","INTERSECT",EDGE,{"derivedFrom":[makeQuery(id+"F4.opChamfer","BLEND_FACE",FACE,{"disambiguationData":[OSD([sQuery(id+"F2.wireOp",EDGE,"E27.0")])]}),makeQuery(id+"F8.opExtrude","SWEPT_FACE",FACE,{"disambiguationData":[OSD([sQuery(id+"F0.wireOp",EDGE,"E5.1.0")])]})]});
            var Q39;
            {var subQ0=sQuery(id+"F0.wireOp",EDGE,"E5.1.0");Q39=makeQuery(id+"F8.boolean.opBoolean","MERGE",EDGE,{"derivedFrom":[makeQuery(id+"F1.opExtrude","SWEPT_EDGE",EDGE,{"disambiguationData":[OSD([subQ0,sQuery(id+"F0.wireOp",EDGE,"E5.1.1")])]}),makeQuery(id+"F8.opExtrude","SWEPT_EDGE",EDGE,{"disambiguationData":[OSD([subQ0,sQuery(id+"F2.wireOp",EDGE,"E27.0")])]})]});}
            fillet(context, id + "F9", {"entities" : qUnion([Q0, Q1, Q2, Q3, Q4, Q5, Q6, Q7, Q8, Q9, Q10, Q11, Q12, Q13, Q14, Q15, Q16, Q17, Q18, Q19, Q20, Q21, Q22, Q23, Q24, Q25, Q26, Q27, Q28, Q29, Q30, Q31, Q32, Q33, Q34, Q35, Q36, Q37, Q38, Q39]), "radius" : .5 * mm, "tangentPropagation" : true, "allowEdgeOverflow" : false});
        }
    });
